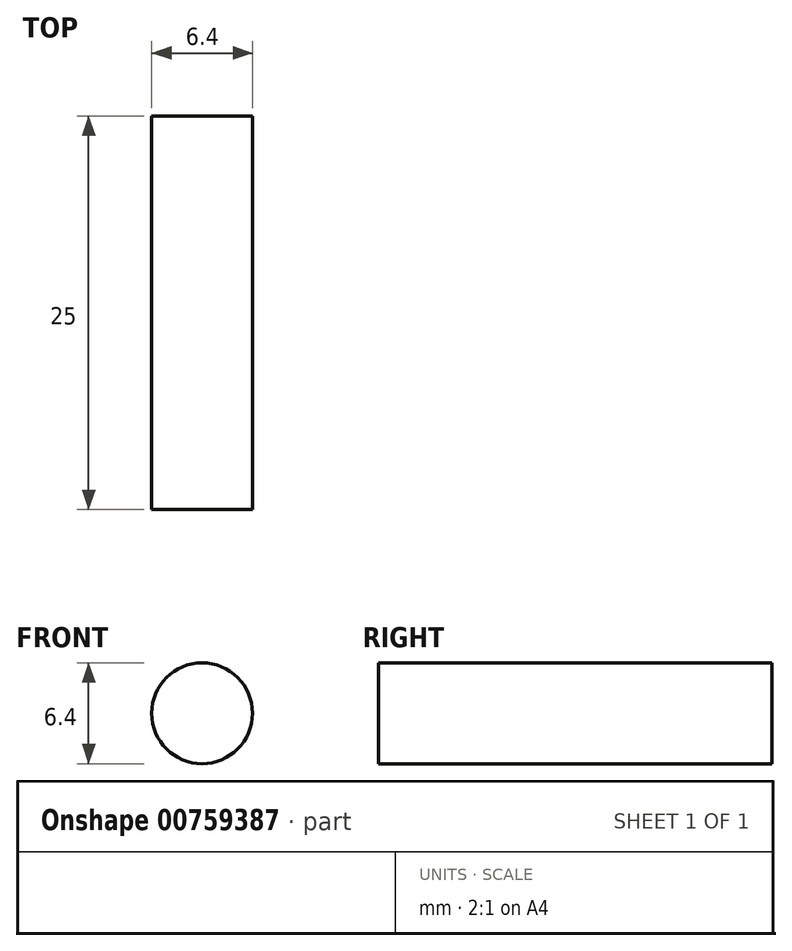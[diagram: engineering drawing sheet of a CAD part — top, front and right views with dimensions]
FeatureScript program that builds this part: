
annotation { "Feature Type Name" : "Feature", "Feature Type Description" : "" }
export const myFeature = defineFeature(function(context is Context, id is Id, definition is map)
    precondition{}
    {
        {
            var Q0;
            Q0=qCreatedBy(makeId("Front.planeOp"),FACE);
            var sketch = newSketch(context, id + "F0", { "sketchPlane" : qUnion([Q0])});
            skCircle(sketch, "E0", {"center": v(0, 0) * mm, "radius": 3.2 * mm});
            skSolve(sketch);
        }
        {
            var Q0;
            Q0=makeQuery(id+"F0.imprint","IMPRINT",FACE,{"disambiguationData":[TD([[makeQuery(id+"F0.imprint","IMPRINT",EDGE,{"derivedFrom":sQuery(id+"F0.wireOp",EDGE,"E0")}),1.0]])]});
            extrude(context, id + "F1", {"entities" : qUnion([Q0]), "oppositeDirection" : true, "depth" : 25 * mm, "offsetDistance" : 25 * mm});
        }
    });
